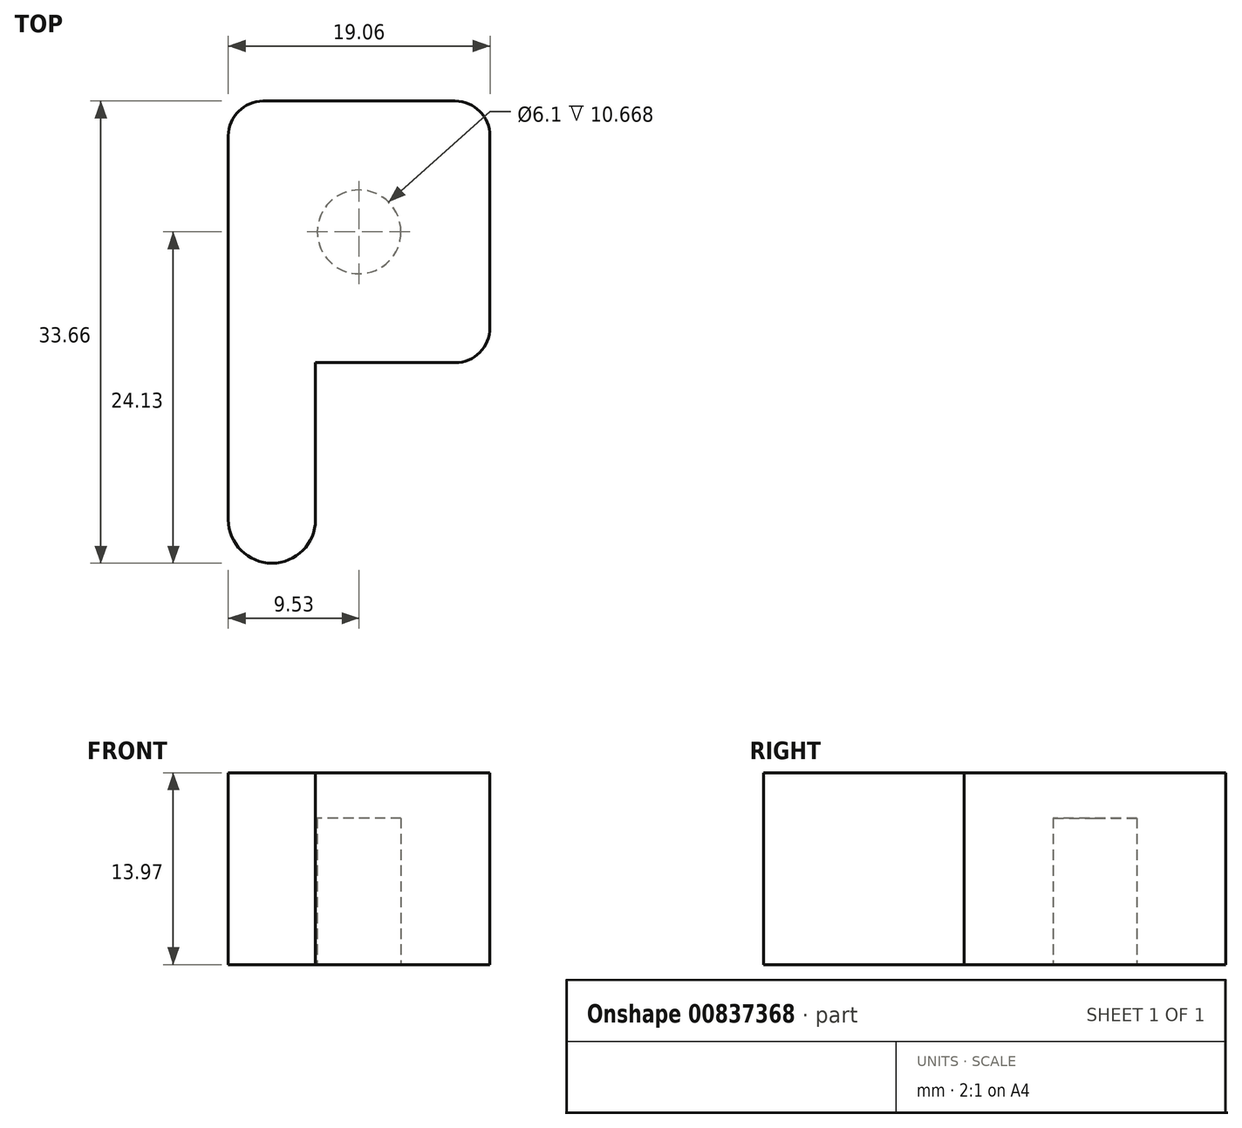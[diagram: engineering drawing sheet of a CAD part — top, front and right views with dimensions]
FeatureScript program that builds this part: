
annotation { "Feature Type Name" : "Feature", "Feature Type Description" : "" }
export const myFeature = defineFeature(function(context is Context, id is Id, definition is map)
    precondition{}
    {
        {
            var Q0;
            Q0=qCreatedBy(makeId("Top.planeOp"),FACE);
            var sketch = newSketch(context, id + "F0", { "sketchPlane" : qUnion([Q0])});
            skCircle(sketch, "E0", {"center": v(0, 0) * mm, "radius": 3.05 * mm});
            skLineSegment(sketch, "E1.bottom", {"start": v(-9.53, 9.53) * mm, "end": v(9.53, 9.53) * mm});
            skLineSegment(sketch, "E1.top", {"start": v(-9.53, -9.52) * mm, "end": v(9.53, -9.52) * mm});
            skLineSegment(sketch, "E1.left", {"start": v(-9.53, 9.53) * mm, "end": v(-9.53, -9.53) * mm});
            skLineSegment(sketch, "E1.right", {"start": v(9.53, 9.53) * mm, "end": v(9.53, -9.53) * mm});
            skLineSegment(sketch, "E2", {"start": v(-9.53, 6.22) * mm, "end": v(9.53, 6.22) * mm});
            skLineSegment(sketch, "E3.left", {"start": v(-9.53, -9.52) * mm, "end": v(-9.53, -20.96) * mm});
            skLineSegment(sketch, "E3.right", {"start": v(-3.18, -9.52) * mm, "end": v(-3.18, -20.96) * mm});
            skArc(sketch, "E4", {"start": v(-9.53, -20.96) * mm, "mid": v(-6.35, -24.13) * mm, "end": v(-3.18, -20.96) * mm});
            skSolve(sketch);
        }
        {
            var Q0;
            Q0=makeQuery(id+"F0.imprint","IMPRINT",FACE,{"disambiguationData":[TD([[makeQuery(id+"F0.imprint","IMPRINT",EDGE,{"derivedFrom":sQuery(id+"F0.wireOp",EDGE,"E0")}),-1.0]])]});
            var Q1;
            {var subQ0=sQuery(id+"F0.wireOp",EDGE,"E1.bottom");Q1=makeQuery(id+"F0.imprint","IMPRINT",FACE,{"disambiguationData":[TD([[makeQuery(id+"F0.imprint","IMPRINT",EDGE,{"derivedFrom":subQ0}),-1.0]])]});}
            extrude(context, id + "F1", {"entities" : qUnion([Q0, Q1]), "depth" : 13.97 * mm, "offsetDistance" : 25.4 * mm});
        }
        {
            var Q0;
            Q0=makeQuery(id+"F1.opExtrude","SWEPT_EDGE",EDGE,{"disambiguationData":[OSD([sQuery(id+"F0.wireOp",EDGE,"E1.bottom"),sQuery(id+"F0.wireOp",EDGE,"E1.right")])]});
            var Q1;
            Q1=makeQuery(id+"F1.opExtrude","SWEPT_EDGE",EDGE,{"disambiguationData":[OSD([sQuery(id+"F0.wireOp",EDGE,"E1.bottom"),sQuery(id+"F0.wireOp",EDGE,"E1.left")])]});
            var Q2;
            Q2=makeQuery(id+"F1.opExtrude","SWEPT_EDGE",EDGE,{"disambiguationData":[OSD([sQuery(id+"F0.wireOp",EDGE,"E1.top"),sQuery(id+"F0.wireOp",EDGE,"E1.right")])]});
            fillet(context, id + "F2", {"entities" : qUnion([Q0, Q1, Q2]), "radius" : 2.54 * mm, "tangentPropagation" : true, "allowEdgeOverflow" : false});
        }
        {
            var Q0;
            Q0=makeQuery(id+"F1.opExtrude","CAP_FACE",FACE,{"disambiguationData":[OSD([sQuery(id+"F0.wireOp",EDGE,"E0"),sQuery(id+"F0.wireOp",EDGE,"E1.bottom"),sQuery(id+"F0.wireOp",EDGE,"E1.top"),sQuery(id+"F0.wireOp",EDGE,"E1.left"),sQuery(id+"F0.wireOp",EDGE,"E1.right")])],"isStart":false});
            var sketch = newSketch(context, id + "F3", { "sketchPlane" : qUnion([Q0])});
            skCircle(sketch, "E5", {"center": v(0, 0) * mm, "radius": 3.05 * mm});
            skSolve(sketch);
        }
        {
            var Q0;
            Q0=qSketchRegion(id+"F3",true);
            extrude(context, id + "F4", {"entities" : qUnion([Q0]), "operationType" : NewBodyOperationType.ADD, "oppositeDirection" : true, "depth" : 3.3 * mm, "offsetDistance" : 25.4 * mm});
        }
        {
            var Q0;
            {var subQ0=sQuery(id+"F0.wireOp",EDGE,"E3.left");Q0=makeQuery(id+"F0.imprint","IMPRINT",FACE,{"disambiguationData":[TD([[makeQuery(id+"F0.imprint","IMPRINT",EDGE,{"derivedFrom":subQ0}),1.0]])]});}
            var Q1;
            Q1=makeQuery(id+"F4.boolean.opBoolean","MERGE",FACE,{"derivedFrom":[makeQuery(id+"F1.opExtrude","CAP_FACE",FACE,{"disambiguationData":[OSD([sQuery(id+"F0.wireOp",EDGE,"E0"),sQuery(id+"F0.wireOp",EDGE,"E1.bottom"),sQuery(id+"F0.wireOp",EDGE,"E1.top"),sQuery(id+"F0.wireOp",EDGE,"E1.left"),sQuery(id+"F0.wireOp",EDGE,"E1.right")])],"isStart":false}),makeQuery(id+"F4.opExtrude","CAP_FACE",FACE,{"disambiguationData":[OSD([sQuery(id+"F3.wireOp",EDGE,"E5")])],"isStart":true})]});
            extrude(context, id + "F5", {"entities" : qUnion([Q0]), "operationType" : NewBodyOperationType.ADD, "endBound" : BoundingType.UP_TO_SURFACE, "depth" : 25.4 * mm, "endBoundEntityFace" : qUnion([Q1]), "offsetDistance" : 25.4 * mm});
        }
    });
